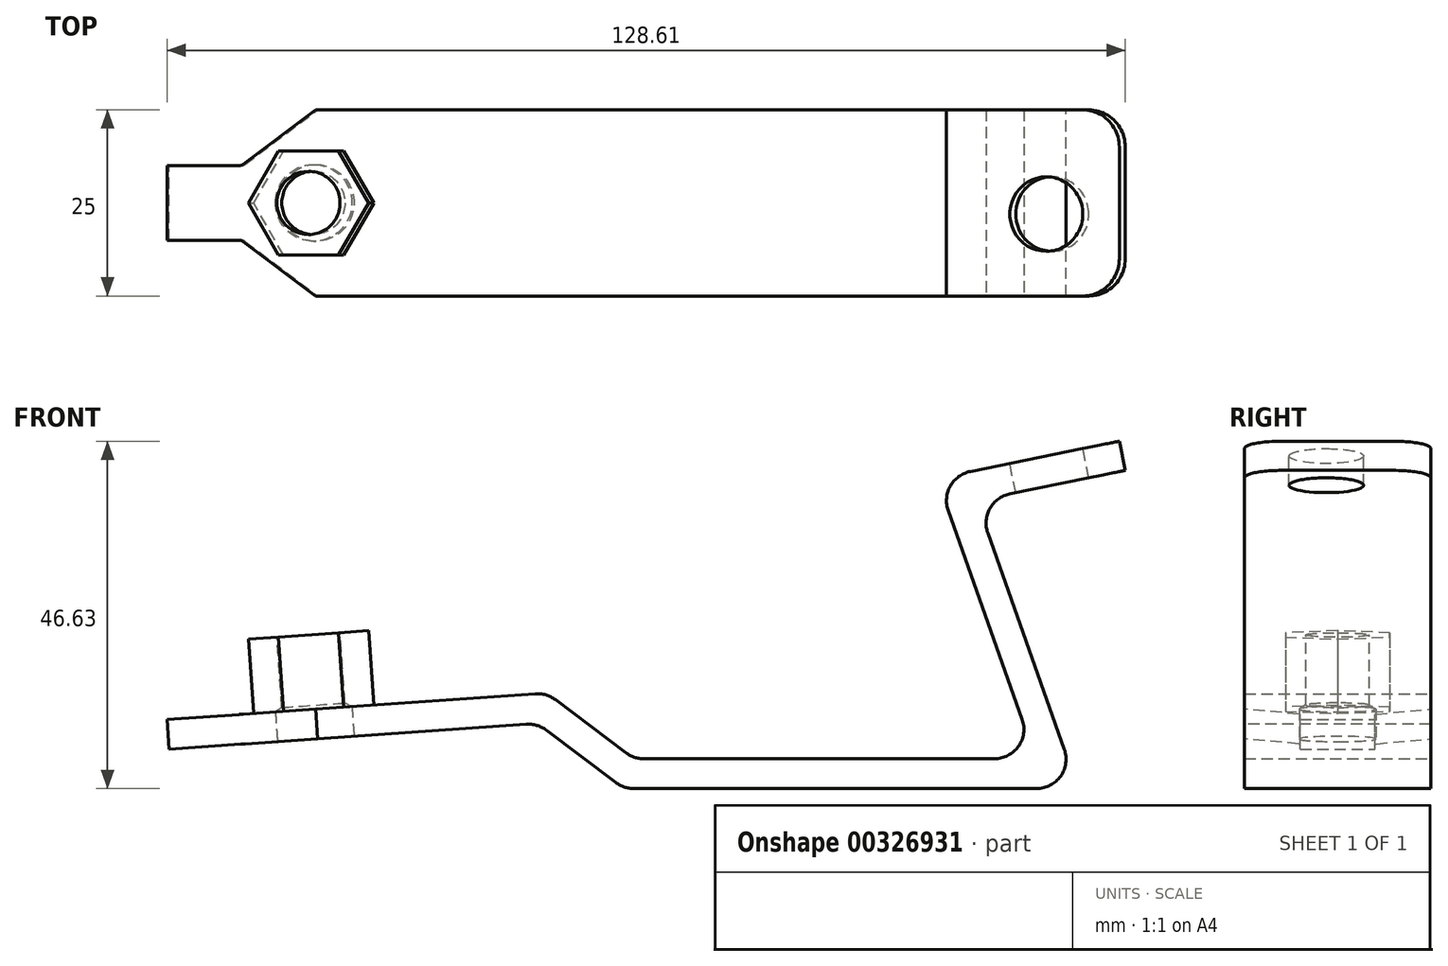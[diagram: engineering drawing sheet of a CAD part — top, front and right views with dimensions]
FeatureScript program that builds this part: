
annotation { "Feature Type Name" : "Feature", "Feature Type Description" : "" }
export const myFeature = defineFeature(function(context is Context, id is Id, definition is map)
    precondition{}
    {
        {
            var Q0;
            Q0=qCreatedBy(makeId("Front.planeOp"),FACE);
            var sketch = newSketch(context, id + "F0", { "sketchPlane" : qUnion([Q0])});
            skLineSegment(sketch, "E0", {"start": v(0, 0) * mm, "end": v(61, 0) * mm});
            skLineSegment(sketch, "E1", {"start": v(61, 0) * mm, "end": v(47.31, 38.65) * mm});
            skLineSegment(sketch, "E2", {"start": v(47.31, 38.65) * mm, "end": v(67.3, 42.72) * mm});
            skLineSegment(sketch, "E3", {"start": v(67.3, 42.72) * mm, "end": v(66.5, 46.63) * mm});
            skLineSegment(sketch, "E4", {"start": v(66.5, 46.63) * mm, "end": v(42, 41.65) * mm});
            skLineSegment(sketch, "E5", {"start": v(42, 41.65) * mm, "end": v(55.34, 4) * mm});
            skLineSegment(sketch, "E6", {"start": v(55.34, 4) * mm, "end": v(1.34, 4) * mm});
            skLineSegment(sketch, "E7", {"start": v(1.34, 4) * mm, "end": v(-10.38, 12.83) * mm});
            skLineSegment(sketch, "E8", {"start": v(-10.38, 12.83) * mm, "end": v(-61.31, 9.27) * mm});
            skLineSegment(sketch, "E9", {"start": v(-61.03, 5.28) * mm, "end": v(-11.6, 8.74) * mm});
            skLineSegment(sketch, "E10", {"start": v(-11.6, 8.74) * mm, "end": v(0, 0) * mm});
            skLineSegment(sketch, "E11", {"start": v(-61.31, 9.27) * mm, "end": v(-61.03, 5.28) * mm});
            skSolve(sketch);
        }
        {
            var Q0;
            Q0 = qSketchRegion(id + "F0", true);
            extrude(context, id + "F1", {"entities" : qUnion([Q0]), "depth" : 25 * mm});
        }
        {
            var Q0;
            Q0=makeQuery(id+"F1.opExtrude","SWEPT_EDGE",EDGE,{"disambiguationData":[OSD([sQuery(id+"F0.wireOp",EDGE,"E4"),sQuery(id+"F0.wireOp",EDGE,"E5")])]});
            var Q1;
            Q1=makeQuery(id+"F1.opExtrude","SWEPT_EDGE",EDGE,{"disambiguationData":[OSD([sQuery(id+"F0.wireOp",EDGE,"E6"),sQuery(id+"F0.wireOp",EDGE,"E7")])]});
            var Q2;
            Q2=makeQuery(id+"F1.opExtrude","SWEPT_EDGE",EDGE,{"disambiguationData":[OSD([sQuery(id+"F0.wireOp",EDGE,"E7"),sQuery(id+"F0.wireOp",EDGE,"E8")])]});
            var Q3;
            Q3=makeQuery(id+"F1.opExtrude","SWEPT_EDGE",EDGE,{"disambiguationData":[OSD([sQuery(id+"F0.wireOp",EDGE,"E9"),sQuery(id+"F0.wireOp",EDGE,"E10")])]});
            var Q4;
            Q4=makeQuery(id+"F1.opExtrude","SWEPT_EDGE",EDGE,{"disambiguationData":[OSD([sQuery(id+"F0.wireOp",EDGE,"E0"),sQuery(id+"F0.wireOp",EDGE,"E10")])]});
            var Q5;
            Q5=makeQuery(id+"F1.opExtrude","SWEPT_EDGE",EDGE,{"disambiguationData":[OSD([sQuery(id+"F0.wireOp",EDGE,"E1"),sQuery(id+"F0.wireOp",EDGE,"E2")])]});
            fillet(context, id + "F2", {"entities" : qUnion([Q0, Q1, Q2, Q3, Q4, Q5]), "radius" : 4 * mm, "tangentPropagation" : true, "allowEdgeOverflow" : false});
        }
        {
            var Q0;
            Q0=makeQuery(id+"F1.opExtrude","SWEPT_EDGE",EDGE,{"disambiguationData":[OSD([sQuery(id+"F0.wireOp",EDGE,"E5"),sQuery(id+"F0.wireOp",EDGE,"E6")])]});
            var Q1;
            Q1=makeQuery(id+"F1.opExtrude","SWEPT_EDGE",EDGE,{"disambiguationData":[OSD([sQuery(id+"F0.wireOp",EDGE,"E0"),sQuery(id+"F0.wireOp",EDGE,"E1")])]});
            fillet(context, id + "F3", {"entities" : qUnion([Q0, Q1]), "radius" : 3.96 * mm, "tangentPropagation" : true, "allowEdgeOverflow" : false});
        }
        {
            var Q0;
            Q0=makeQuery(id+"F1.opExtrude","CAP_EDGE",EDGE,{"disambiguationData":[OSD([sQuery(id+"F0.wireOp",EDGE,"E3")])],"isStart":false});
            var Q1;
            Q1=makeQuery(id+"F1.opExtrude","CAP_EDGE",EDGE,{"disambiguationData":[OSD([sQuery(id+"F0.wireOp",EDGE,"E3")])],"isStart":true});
            fillet(context, id + "F4", {"entities" : qUnion([Q0, Q1]), "radius" : 5 * mm, "tangentPropagation" : true, "allowEdgeOverflow" : false});
        }
        {
            var Q0;
            Q0=makeQuery(id+"F1.opExtrude","SWEPT_FACE",FACE,{"disambiguationData":[OSD([sQuery(id+"F0.wireOp",EDGE,"E8")])]});
            var sketch = newSketch(context, id + "F5", { "sketchPlane" : qUnion([Q0])});
            skLineSegment(sketch, "E12.bottom", {"start": v(-60.52, -7.5) * mm, "end": v(-50.52, -7.5) * mm});
            skLineSegment(sketch, "E12.top", {"start": v(-60.52, -17.5) * mm, "end": v(-50.52, -17.5) * mm});
            skLineSegment(sketch, "E12.left", {"start": v(-60.52, -7.5) * mm, "end": v(-60.52, -17.5) * mm});
            skLineSegment(sketch, "E13", {"start": v(-50.52, -7.5) * mm, "end": v(-40.52, 0) * mm});
            skLineSegment(sketch, "E14", {"start": v(-50.52, -17.5) * mm, "end": v(-40.52, -25) * mm});
            skSolve(sketch);
        }
        {
            var Q0;
            {var subQ0=sQuery(id+"F5.wireOp",EDGE,"E12.bottom");Q0=makeQuery(id+"F5.imprint","IMPRINT",FACE,{"disambiguationData":[TD([[makeQuery(id+"F5.imprint","IMPRINT",EDGE,{"derivedFrom":subQ0}),1.0]])]});}
            var Q1;
            {var subQ0=sQuery(id+"F5.wireOp",EDGE,"E12.top");Q1=makeQuery(id+"F5.imprint","IMPRINT",FACE,{"disambiguationData":[TD([[makeQuery(id+"F5.imprint","IMPRINT",EDGE,{"derivedFrom":subQ0}),-1.0]])]});}
            extrude(context, id + "F6", {"entities" : qUnion([Q0, Q1]), "operationType" : NewBodyOperationType.REMOVE, "oppositeDirection" : true, "depth" : 4 * mm});
        }
        {
            var Q0;
            Q0=makeQuery(id+"F6.boolean.opBoolean","COPY",EDGE,{"derivedFrom":makeQuery(id+"F6.opExtrude","SWEPT_EDGE",EDGE,{"disambiguationData":[OSD([sQuery(id+"F0.wireOp",EDGE,"E8"),sQuery(id+"F5.wireOp",EDGE,"E14")])]})});
            var Q1;
            Q1=makeQuery(id+"F6.boolean.opBoolean","COPY",EDGE,{"derivedFrom":makeQuery(id+"F6.opExtrude","SWEPT_EDGE",EDGE,{"disambiguationData":[OSD([sQuery(id+"F5.wireOp",EDGE,"E12.top"),sQuery(id+"F5.wireOp",EDGE,"E14")])]})});
            var Q2;
            Q2=makeQuery(id+"F6.boolean.opBoolean","COPY",EDGE,{"derivedFrom":makeQuery(id+"F6.opExtrude","SWEPT_EDGE",EDGE,{"disambiguationData":[OSD([sQuery(id+"F0.wireOp",EDGE,"E8"),sQuery(id+"F0.wireOp",EDGE,"E11"),sQuery(id+"F5.wireOp",EDGE,"E12.top"),sQuery(id+"F5.wireOp",EDGE,"E12.left")])]})});
            var Q3;
            Q3=makeQuery(id+"F6.boolean.opBoolean","COPY",EDGE,{"derivedFrom":makeQuery(id+"F6.opExtrude","SWEPT_EDGE",EDGE,{"disambiguationData":[OSD([sQuery(id+"F0.wireOp",EDGE,"E8"),sQuery(id+"F0.wireOp",EDGE,"E11"),sQuery(id+"F5.wireOp",EDGE,"E12.bottom"),sQuery(id+"F5.wireOp",EDGE,"E12.left")])]})});
            var Q4;
            Q4=makeQuery(id+"F6.boolean.opBoolean","COPY",EDGE,{"derivedFrom":makeQuery(id+"F6.opExtrude","SWEPT_EDGE",EDGE,{"disambiguationData":[OSD([sQuery(id+"F0.wireOp",EDGE,"E8"),sQuery(id+"F5.wireOp",EDGE,"E13")])]})});
            var Q5;
            Q5=makeQuery(id+"F6.boolean.opBoolean","COPY",EDGE,{"derivedFrom":makeQuery(id+"F6.opExtrude","SWEPT_EDGE",EDGE,{"disambiguationData":[OSD([sQuery(id+"F5.wireOp",EDGE,"E12.bottom"),sQuery(id+"F5.wireOp",EDGE,"E13")])]})});
            fillet(context, id + "F7", {"entities" : qUnion([Q0, Q1, Q2, Q3, Q4, Q5]), "radius" : 1 * mm, "tangentPropagation" : true, "allowEdgeOverflow" : false});
        }
        {
            var Q0;
            Q0=makeQuery(id+"F1.opExtrude","SWEPT_FACE",FACE,{"disambiguationData":[OSD([sQuery(id+"F0.wireOp",EDGE,"E8")])]});
            var sketch = newSketch(context, id + "F8", { "sketchPlane" : qUnion([Q0])});
            skCircle(sketch, "E15.cCircle", {"center": v(-40.78, -12.5) * mm, "radius": 7 * mm, "construction": true});
            skPoint(sketch, "E15.cCircle.centerSnap0", {"position": v(-60.52, -12.5) * mm});
            skLineSegment(sketch, "E15.0", {"start": v(-32.7, -12.5) * mm, "end": v(-36.74, -19.5) * mm});
            skLineSegment(sketch, "E15.1", {"start": v(-36.74, -19.5) * mm, "end": v(-44.82, -19.5) * mm});
            skLineSegment(sketch, "E15.2", {"start": v(-44.82, -19.5) * mm, "end": v(-48.87, -12.5) * mm});
            skLineSegment(sketch, "E15.3", {"start": v(-48.87, -12.5) * mm, "end": v(-44.82, -5.5) * mm});
            skLineSegment(sketch, "E15.4", {"start": v(-44.82, -5.5) * mm, "end": v(-36.74, -5.5) * mm});
            skLineSegment(sketch, "E15.5", {"start": v(-36.74, -5.5) * mm, "end": v(-32.7, -12.5) * mm});
            skPoint(sketch, "E15.0.midPoint", {"position": v(-34.72, -16) * mm});
            skSolve(sketch);
        }
        {
            var Q0;
            Q0=makeQuery(id+"F8.imprint","IMPRINT",FACE,{"disambiguationData":[TD([[makeQuery(id+"F8.imprint","IMPRINT",EDGE,{"derivedFrom":sQuery(id+"F8.wireOp",EDGE,"E15.0")}),-1.0]])]});
            extrude(context, id + "F9", {"entities" : qUnion([Q0]), "operationType" : NewBodyOperationType.ADD, "depth" : 10 * mm});
        }
        {
            var Q0;
            Q0=makeQuery(id+"F9.opExtrude","CAP_FACE",FACE,{"disambiguationData":[OSD([sQuery(id+"F8.wireOp",EDGE,"E15.0"),sQuery(id+"F8.wireOp",EDGE,"E15.1"),sQuery(id+"F8.wireOp",EDGE,"E15.2"),sQuery(id+"F8.wireOp",EDGE,"E15.3"),sQuery(id+"F8.wireOp",EDGE,"E15.4"),sQuery(id+"F8.wireOp",EDGE,"E15.5")])],"isStart":false});
            var sketch = newSketch(context, id + "F10", { "sketchPlane" : qUnion([Q0])});
            skPoint(sketch, "E16", {"position": v(-40.78, -5.5) * mm});
            skPoint(sketch, "E17", {"position": v(-40.78, -12.5) * mm});
            skSolve(sketch);
        }
        {
            var Q0;
            Q0=sQuery(id+"F10.wireOp",VERTEX,"E17");
            var Q1;
            Q1=makeQuery(id+"F1.opExtrude","SWEPT_BODY",BODY,{"disambiguationData":[OSD([sQuery(id+"F0.wireOp",EDGE,"E0"),sQuery(id+"F0.wireOp",EDGE,"E1"),sQuery(id+"F0.wireOp",EDGE,"E2"),sQuery(id+"F0.wireOp",EDGE,"E3"),sQuery(id+"F0.wireOp",EDGE,"E4"),sQuery(id+"F0.wireOp",EDGE,"E5"),sQuery(id+"F0.wireOp",EDGE,"E6"),sQuery(id+"F0.wireOp",EDGE,"E7"),sQuery(id+"F0.wireOp",EDGE,"E8"),sQuery(id+"F0.wireOp",EDGE,"E9"),sQuery(id+"F0.wireOp",EDGE,"E10"),sQuery(id+"F0.wireOp",EDGE,"E11")])]});
            hole(context, id + "F11", {"style" : HoleStyle.SIMPLE, "endStyle" : HoleEndStyle.BLIND, "holeDiameter" : 8.5 * mm, "holeDepth" : 20 * mm, "isTappedThrough" : true, "tappedDepth" : 12 * mm, "tapClearance" : 3, "startFromSketch" : true, "locations" : qUnion([Q0]), "scope" : qUnion([Q1])});
        }
        {
            var Q0;
            Q0=makeQuery(id+"F1.opExtrude","SWEPT_FACE",FACE,{"disambiguationData":[OSD([sQuery(id+"F0.wireOp",EDGE,"E9")])]});
            var sketch = newSketch(context, id + "F12", { "sketchPlane" : qUnion([Q0])});
            skPoint(sketch, "E18", {"position": v(-40.78, 12.5) * mm});
            skSolve(sketch);
        }
        {
            var Q0;
            Q0=sQuery(id+"F12.wireOp",VERTEX,"E18");
            var Q1;
            Q1=makeQuery(id+"F1.opExtrude","SWEPT_BODY",BODY,{"disambiguationData":[OSD([sQuery(id+"F0.wireOp",EDGE,"E0"),sQuery(id+"F0.wireOp",EDGE,"E1"),sQuery(id+"F0.wireOp",EDGE,"E2"),sQuery(id+"F0.wireOp",EDGE,"E3"),sQuery(id+"F0.wireOp",EDGE,"E4"),sQuery(id+"F0.wireOp",EDGE,"E5"),sQuery(id+"F0.wireOp",EDGE,"E6"),sQuery(id+"F0.wireOp",EDGE,"E7"),sQuery(id+"F0.wireOp",EDGE,"E8"),sQuery(id+"F0.wireOp",EDGE,"E9"),sQuery(id+"F0.wireOp",EDGE,"E10"),sQuery(id+"F0.wireOp",EDGE,"E11")])]});
            hole(context, id + "F13", {"style" : HoleStyle.SIMPLE, "endStyle" : HoleEndStyle.BLIND, "holeDiameter" : 10.3 * mm, "holeDepth" : 4 * mm, "isTappedThrough" : true, "tappedDepth" : 12 * mm, "tapClearance" : 3, "startFromSketch" : true, "locations" : qUnion([Q0]), "scope" : qUnion([Q1])});
        }
        {
            var Q0;
            Q0=makeQuery(id+"F1.opExtrude","SWEPT_FACE",FACE,{"disambiguationData":[OSD([sQuery(id+"F0.wireOp",EDGE,"E4")])]});
            var sketch = newSketch(context, id + "F14", { "sketchPlane" : qUnion([Q0])});
            skPoint(sketch, "E19", {"position": v(64.47, -14) * mm});
            skSolve(sketch);
        }
        {
            var Q0;
            Q0=sQuery(id+"F14.wireOp",VERTEX,"E19");
            var Q1;
            Q1=makeQuery(id+"F1.opExtrude","SWEPT_BODY",BODY,{"disambiguationData":[OSD([sQuery(id+"F0.wireOp",EDGE,"E0"),sQuery(id+"F0.wireOp",EDGE,"E1"),sQuery(id+"F0.wireOp",EDGE,"E2"),sQuery(id+"F0.wireOp",EDGE,"E3"),sQuery(id+"F0.wireOp",EDGE,"E4"),sQuery(id+"F0.wireOp",EDGE,"E5"),sQuery(id+"F0.wireOp",EDGE,"E6"),sQuery(id+"F0.wireOp",EDGE,"E7"),sQuery(id+"F0.wireOp",EDGE,"E8"),sQuery(id+"F0.wireOp",EDGE,"E9"),sQuery(id+"F0.wireOp",EDGE,"E10"),sQuery(id+"F0.wireOp",EDGE,"E11")])]});
            hole(context, id + "F15", {"style" : HoleStyle.SIMPLE, "endStyle" : HoleEndStyle.BLIND, "holeDiameter" : 10 * mm, "holeDepth" : 4 * mm, "isTappedThrough" : true, "tappedDepth" : 12 * mm, "tapClearance" : 3, "startFromSketch" : true, "locations" : qUnion([Q0]), "scope" : qUnion([Q1])});
        }
    });
